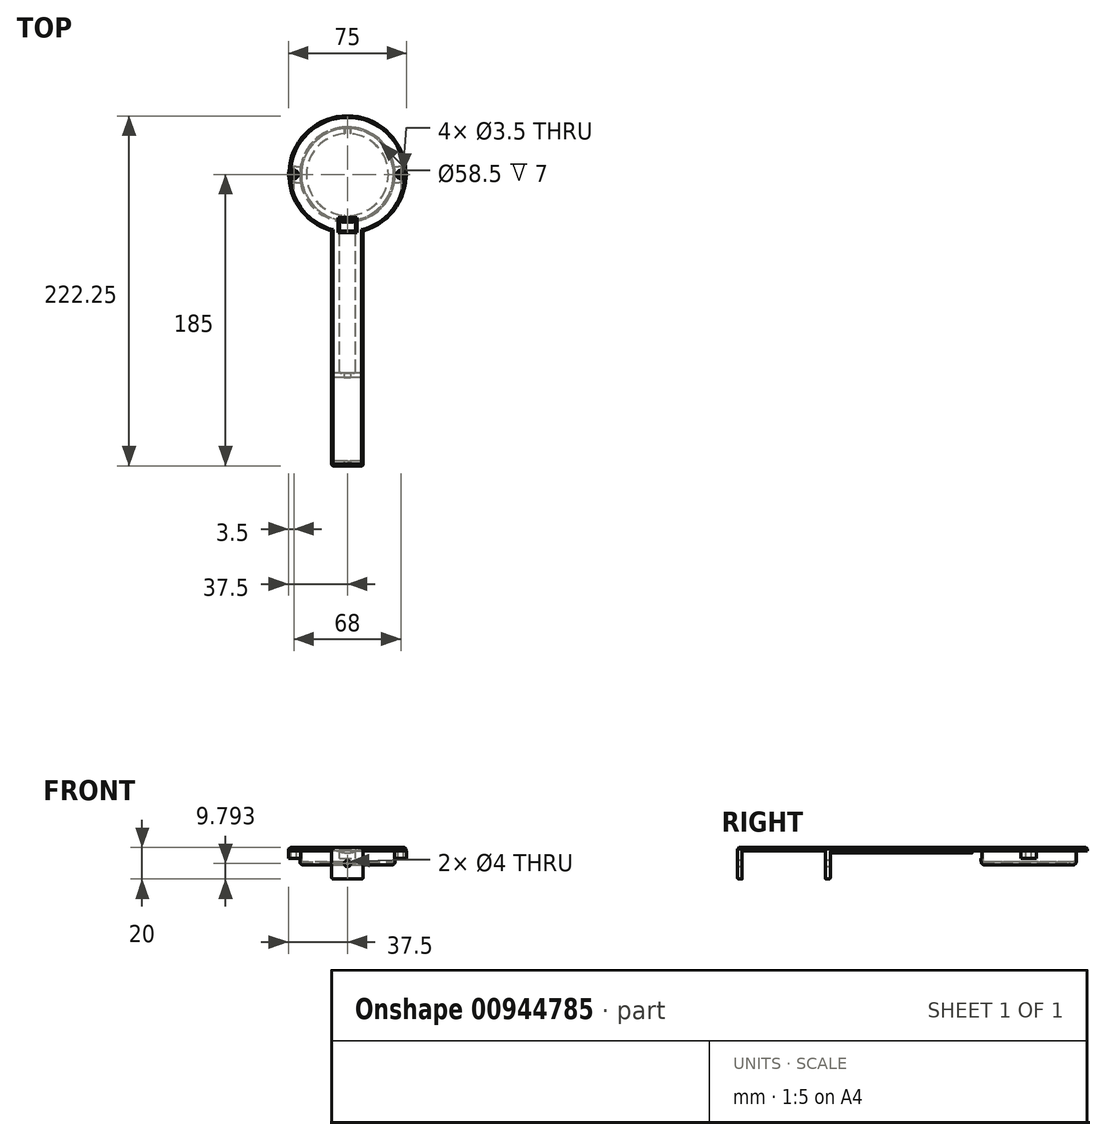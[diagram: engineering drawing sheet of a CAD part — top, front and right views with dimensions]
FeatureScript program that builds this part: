
annotation { "Feature Type Name" : "Feature", "Feature Type Description" : "" }
export const myFeature = defineFeature(function(context is Context, id is Id, definition is map)
    precondition{}
    {
        {
            var Q0;
            Q0=qCreatedBy(makeId("Top.planeOp"),FACE);
            var sketch = newSketch(context, id + "F0", { "sketchPlane" : qUnion([Q0])});
            skCircle(sketch, "E0", {"center": v(0, 0) * mm, "radius": 26 * mm});
            skCircle(sketch, "E1", {"center": v(0, 0) * mm, "radius": 29.25 * mm});
            skCircle(sketch, "E2", {"center": v(0, 0) * mm, "radius": 30.25 * mm});
            skSolve(sketch);
        }
        {
            var Q0;
            Q0=makeQuery(id+"F0.imprint","IMPRINT",FACE,{"disambiguationData":[TD([[makeQuery(id+"F0.imprint","IMPRINT",EDGE,{"derivedFrom":sQuery(id+"F0.wireOp",EDGE,"E0")}),-1.0]])]});
            extrude(context, id + "F1", {"entities" : qUnion([Q0]), "depth" : 2 * mm, "offsetDistance" : 25 * mm});
        }
        {
            var Q0;
            Q0 = qSketchRegion(id + "F0", true);
            extrude(context, id + "F2", {"entities" : qUnion([Q0]), "operationType" : NewBodyOperationType.ADD, "depth" : 9 * mm, "offsetDistance" : 25 * mm});
        }
        {
            var Q0;
            Q0=makeQuery(id+"F2.opExtrude","CAP_FACE",FACE,{"disambiguationData":[OSD([sQuery(id+"F0.wireOp",EDGE,"E1"),sQuery(id+"F0.wireOp",EDGE,"E2")])],"isStart":false});
            var sketch = newSketch(context, id + "F3", { "sketchPlane" : qUnion([Q0])});
            skPoint(sketch, "E3.0", {"position": v(0, 0) * mm});
            skCircle(sketch, "E4", {"center": v(0, 0) * mm, "radius": 29.25 * mm});
            skCircle(sketch, "E5", {"center": v(0, 0) * mm, "radius": 37.25 * mm});
            skLineSegment(sketch, "E6.bottom", {"start": v(-36.3, 8.33) * mm, "end": v(36.3, 8.33) * mm});
            skLineSegment(sketch, "E6.top", {"start": v(-36.3, -8.33) * mm, "end": v(36.3, -8.33) * mm});
            skLineSegment(sketch, "E6.left", {"start": v(-36.3, 8.33) * mm, "end": v(-36.3, -8.33) * mm});
            skLineSegment(sketch, "E6.right", {"start": v(36.3, 8.33) * mm, "end": v(36.3, -8.33) * mm});
            skLineSegment(sketch, "E7.bottom", {"start": v(-5, 36.91) * mm, "end": v(5, 36.91) * mm});
            skLineSegment(sketch, "E7.top", {"start": v(-5, -36.91) * mm, "end": v(5, -36.91) * mm});
            skLineSegment(sketch, "E7.left", {"start": v(-5, 36.91) * mm, "end": v(-5, -36.91) * mm});
            skLineSegment(sketch, "E7.right", {"start": v(5, 36.91) * mm, "end": v(5, -36.91) * mm});
            skSolve(sketch);
        }
        {
            var Q0;
            Q0=makeQuery(id+"F2.opExtrude","CAP_EDGE",EDGE,{"disambiguationData":[OSD([sQuery(id+"F0.wireOp",EDGE,"E2")])],"isStart":true});
            fillet(context, id + "F4", {"entities" : qUnion([Q0]), "radius" : 2 * mm, "tangentPropagation" : true, "allowEdgeOverflow" : false});
        }
        {
            var Q0;
            Q0=makeQuery(id+"F2.opExtrude","CAP_FACE",FACE,{"disambiguationData":[OSD([sQuery(id+"F0.wireOp",EDGE,"E1"),sQuery(id+"F0.wireOp",EDGE,"E2")])],"isStart":false});
            var sketch = newSketch(context, id + "F5", { "sketchPlane" : qUnion([Q0])});
            skPoint(sketch, "E8.0", {"position": v(0, 0) * mm});
            skLineSegment(sketch, "E9.bottom", {"start": v(-37.5, 5) * mm, "end": v(37.5, 5) * mm});
            skLineSegment(sketch, "E9.top", {"start": v(-37.5, -5) * mm, "end": v(37.5, -5) * mm});
            skLineSegment(sketch, "E9.left", {"start": v(-37.5, 5) * mm, "end": v(-37.5, -5) * mm});
            skLineSegment(sketch, "E9.right", {"start": v(37.5, 5) * mm, "end": v(37.5, -5) * mm});
            skLineSegment(sketch, "E10", {"start": v(-37.5, 0) * mm, "end": v(-34, 0) * mm, "construction": true});
            skLineSegment(sketch, "E11", {"start": v(37.5, 0) * mm, "end": v(34, 0) * mm, "construction": true});
            skCircle(sketch, "E12", {"center": v(-34, 0) * mm, "radius": 1.75 * mm});
            skCircle(sketch, "E13", {"center": v(34, 0) * mm, "radius": 1.75 * mm});
            skLineSegment(sketch, "E14.bottom", {"start": v(5, -45) * mm, "end": v(-5, -45) * mm});
            skLineSegment(sketch, "E14.top", {"start": v(5, 45) * mm, "end": v(-5, 45) * mm});
            skLineSegment(sketch, "E14.left", {"start": v(5, -45) * mm, "end": v(5, 45) * mm});
            skLineSegment(sketch, "E14.right", {"start": v(-5, -45) * mm, "end": v(-5, 45) * mm});
            skSolve(sketch);
        }
        {
            var Q0;
            {var subQ0=sQuery(id+"F5.wireOp",EDGE,"E9.left");Q0=makeQuery(id+"F5.imprint","IMPRINT",FACE,{"disambiguationData":[TD([[makeQuery(id+"F5.imprint","IMPRINT",EDGE,{"derivedFrom":subQ0}),1.0]])]});}
            var Q1;
            {var subQ0=sQuery(id+"F5.wireOp",EDGE,"E9.right");Q1=makeQuery(id+"F5.imprint","IMPRINT",FACE,{"disambiguationData":[TD([[makeQuery(id+"F5.imprint","IMPRINT",EDGE,{"derivedFrom":subQ0}),-1.0]])]});}
            extrude(context, id + "F6", {"entities" : qUnion([Q0, Q1]), "operationType" : NewBodyOperationType.ADD, "oppositeDirection" : true, "depth" : 5 * mm, "offsetDistance" : 25 * mm});
        }
        {
            var Q0;
            Q0=makeQuery(id+"F6.opExtrude","SWEPT_EDGE",EDGE,{"disambiguationData":[OSD([sQuery(id+"F5.wireOp",EDGE,"E9.top"),sQuery(id+"F5.wireOp",EDGE,"E9.right")])]});
            var Q1;
            Q1=makeQuery(id+"F6.opExtrude","SWEPT_EDGE",EDGE,{"disambiguationData":[OSD([sQuery(id+"F5.wireOp",EDGE,"E9.bottom"),sQuery(id+"F5.wireOp",EDGE,"E9.right")])]});
            var Q2;
            Q2=makeQuery(id+"F6.opExtrude","SWEPT_EDGE",EDGE,{"disambiguationData":[OSD([sQuery(id+"F5.wireOp",EDGE,"E9.top"),sQuery(id+"F5.wireOp",EDGE,"E9.left")])]});
            var Q3;
            Q3=makeQuery(id+"F6.opExtrude","SWEPT_EDGE",EDGE,{"disambiguationData":[OSD([sQuery(id+"F5.wireOp",EDGE,"E9.bottom"),sQuery(id+"F5.wireOp",EDGE,"E9.left")])]});
            fillet(context, id + "F7", {"entities" : qUnion([Q0, Q1, Q2, Q3]), "radius" : 5 * mm, "tangentPropagation" : true, "allowEdgeOverflow" : false});
        }
        {
            var Q0;
            {var subQ0=sQuery(id+"F5.wireOp",EDGE,"E14.left");var subQ1=makeQuery(id+"F2.opExtrude","CAP_EDGE",EDGE,{"disambiguationData":[OSD([sQuery(id+"F0.wireOp",EDGE,"E2")])],"isStart":false});var subQ2=makeQuery(id+"F5.imprint","INTERSECT",VERTEX,{"disambiguationData":[OD(0.0)],"derivedFrom":[subQ1,subQ0]});Q0=makeQuery(id+"F5.imprint","IMPRINT",FACE,{"disambiguationData":[TD([[makeQuery(id+"F5.imprint","IMPRINT",EDGE,{"disambiguationData":[TD([[subQ2,-1.0]])],"derivedFrom":subQ0}),1.0]])]});}
            extrude(context, id + "F8", {"entities" : qUnion([Q0]), "operationType" : NewBodyOperationType.REMOVE, "oppositeDirection" : true, "depth" : 5 * mm, "offsetDistance" : 25 * mm});
        }
        {
            var Q0;
            {var subQ0=sQuery(id+"F3.wireOp",EDGE,"E7.left");var subQ1=sQuery(id+"F3.wireOp",EDGE,"E6.bottom");var subQ2=makeQuery(id+"F3.imprint","INTERSECT",VERTEX,{"derivedFrom":[subQ1,subQ0]});Q0=makeQuery(id+"F3.imprint","IMPRINT",FACE,{"disambiguationData":[TD([[makeQuery(id+"F3.imprint","IMPRINT",EDGE,{"disambiguationData":[TD([[subQ2,-1.0]])],"derivedFrom":subQ1}),-1.0]])]});}
            var sketch = newSketch(context, id + "F9", { "sketchPlane" : qUnion([Q0])});
            skCircle(sketch, "E15.0", {"center": v(0, 0) * mm, "radius": 37.25 * mm});
            skCircle(sketch, "E15.1", {"center": v(-34, 0) * mm, "radius": 1.75 * mm});
            skCircle(sketch, "E15.2", {"center": v(34, 0) * mm, "radius": 1.75 * mm});
            skPoint(sketch, "E15.3", {"position": v(0, 0) * mm});
            skSolve(sketch);
        }
        {
            var Q0;
            Q0=makeQuery(id+"F9.imprint","IMPRINT",FACE,{"disambiguationData":[TD([[makeQuery(id+"F9.imprint","IMPRINT",EDGE,{"derivedFrom":sQuery(id+"F9.wireOp",EDGE,"E15.0")}),1.0]])]});
            var Q1;
            {var subQ0=sQuery(id+"F3.wireOp",EDGE,"E7.left");var subQ1=sQuery(id+"F3.wireOp",EDGE,"E6.bottom");var subQ2=makeQuery(id+"F3.imprint","INTERSECT",VERTEX,{"derivedFrom":[subQ1,subQ0]});Q1=makeQuery(id+"F9.imprint","IMPRINT",FACE,{"disambiguationData":[TD([[makeQuery(id+"F9.imprint","IMPRINT",EDGE,{"derivedFrom":makeQuery(id+"F3.imprint","IMPRINT",EDGE,{"disambiguationData":[TD([[subQ2,-1.0]])],"derivedFrom":subQ1})}),-1.0]])]});}
            extrude(context, id + "F10", {"entities" : qUnion([Q0, Q1]), "depth" : 2 * mm, "offsetDistance" : 25 * mm});
        }
        {
            var Q0;
            Q0=makeQuery(id+"F10.opExtrude","CAP_FACE",FACE,{"disambiguationData":[OSD([sQuery(id+"F9.wireOp",EDGE,"E15.0"),sQuery(id+"F9.wireOp",EDGE,"E15.1"),sQuery(id+"F9.wireOp",EDGE,"E15.2")])],"isStart":false});
            var sketch = newSketch(context, id + "F11", { "sketchPlane" : qUnion([Q0])});
            skLineSegment(sketch, "E16", {"start": v(34, 0) * mm, "end": v(-34, 0) * mm, "construction": true});
            skPoint(sketch, "E17.0", {"position": v(0, 0) * mm});
            skLineSegment(sketch, "E18", {"start": v(0, 0) * mm, "end": v(-10, 0) * mm, "construction": true});
            skLineSegment(sketch, "E19", {"start": v(0, 0) * mm, "end": v(10, 0) * mm, "construction": true});
            skLineSegment(sketch, "E20", {"start": v(-10, 0) * mm, "end": v(-10, 15) * mm, "construction": true});
            skLineSegment(sketch, "E21", {"start": v(-10, 15) * mm, "end": v(10, 15) * mm, "construction": true});
            skLineSegment(sketch, "E22.bottom", {"start": v(-10, 15) * mm, "end": v(10, 15) * mm});
            skLineSegment(sketch, "E22.top", {"start": v(-10, -185) * mm, "end": v(10, -185) * mm});
            skLineSegment(sketch, "E22.left", {"start": v(-10, 15) * mm, "end": v(-10, -185) * mm});
            skLineSegment(sketch, "E22.right", {"start": v(10, 15) * mm, "end": v(10, -185) * mm});
            skSolve(sketch);
        }
        {
            var Q0;
            {var subQ0=sQuery(id+"F11.wireOp",EDGE,"E22.top");Q0=makeQuery(id+"F11.imprint","IMPRINT",FACE,{"disambiguationData":[TD([[makeQuery(id+"F11.imprint","IMPRINT",EDGE,{"derivedFrom":subQ0}),1.0]])]});}
            extrude(context, id + "F12", {"entities" : qUnion([Q0]), "operationType" : NewBodyOperationType.ADD, "oppositeDirection" : true, "depth" : 2 * mm, "offsetDistance" : 25 * mm});
        }
        {
            var Q0;
            Q0=makeQuery(id+"F9.imprint","IMPRINT",FACE,{"disambiguationData":[TD([[makeQuery(id+"F9.imprint","IMPRINT",EDGE,{"derivedFrom":sQuery(id+"F9.wireOp",EDGE,"E15.0")}),1.0]])]});
            var sketch = newSketch(context, id + "F13", { "sketchPlane" : qUnion([Q0])});
            skLineSegment(sketch, "E23", {"start": v(0, 9.04) * mm, "end": v(0, -35.96) * mm, "construction": true});
            skLineSegment(sketch, "E24.bottom", {"start": v(5, -28.46) * mm, "end": v(-5, -28.46) * mm});
            skPoint(sketch, "E24.middle", {"position": v(0, -35.96) * mm});
            skLineSegment(sketch, "E25", {"start": v(5, -35.96) * mm, "end": v(-5, -35.96) * mm});
            skLineSegment(sketch, "E26", {"start": v(5, -28.46) * mm, "end": v(5, -35.96) * mm});
            skLineSegment(sketch, "E27", {"start": v(-5, -35.96) * mm, "end": v(-5, -28.46) * mm});
            skSolve(sketch);
        }
        {
            var Q0;
            Q0=makeQuery(id+"F13.imprint","IMPRINT",FACE,{"disambiguationData":[TD([[makeQuery(id+"F13.imprint","IMPRINT",EDGE,{"derivedFrom":sQuery(id+"F13.wireOp",EDGE,"E24.bottom")}),1.0]])]});
            extrude(context, id + "F14", {"entities" : qUnion([Q0]), "operationType" : NewBodyOperationType.REMOVE, "endBound" : BoundingType.UP_TO_NEXT, "depth" : 25 * mm, "offsetDistance" : 25 * mm});
        }
        {
            var Q0;
            {var subQ0=sQuery(id+"F9.wireOp",EDGE,"E15.0");Q0=makeQuery(id+"F12.boolean.opBoolean","MERGE",FACE,{"derivedFrom":[makeQuery(id+"F10.opExtrude","CAP_FACE",FACE,{"disambiguationData":[OSD([subQ0,sQuery(id+"F9.wireOp",EDGE,"E15.1"),sQuery(id+"F9.wireOp",EDGE,"E15.2")])],"isStart":false}),makeQuery(id+"F12.opExtrude","CAP_FACE",FACE,{"disambiguationData":[OSD([subQ0,sQuery(id+"F11.wireOp",EDGE,"E22.top"),sQuery(id+"F11.wireOp",EDGE,"E22.left"),sQuery(id+"F11.wireOp",EDGE,"E22.right")])],"isStart":true})]});}
            chamfer(context, id + "F15", {"entities" : qUnion([Q0]), "chamferType" : ChamferType.OFFSET_ANGLE, "width" : 1 * mm, "oppositeDirection" : false, "angle" : 45 * degree, "tangentPropagation" : true});
        }
        {
            var Q0;
            {var subQ0=sQuery(id+"F9.wireOp",EDGE,"E15.0");Q0=makeQuery(id+"F12.boolean.opBoolean","MERGE",FACE,{"derivedFrom":[makeQuery(id+"F10.opExtrude","CAP_FACE",FACE,{"disambiguationData":[OSD([subQ0,sQuery(id+"F9.wireOp",EDGE,"E15.1"),sQuery(id+"F9.wireOp",EDGE,"E15.2")])],"isStart":true}),makeQuery(id+"F12.opExtrude","CAP_FACE",FACE,{"disambiguationData":[OSD([subQ0,sQuery(id+"F11.wireOp",EDGE,"E22.top"),sQuery(id+"F11.wireOp",EDGE,"E22.left"),sQuery(id+"F11.wireOp",EDGE,"E22.right")])],"isStart":false})]});}
            var sketch = newSketch(context, id + "F16", { "sketchPlane" : qUnion([Q0])});
            skLineSegment(sketch, "E28.bottom", {"start": v(10, 185) * mm, "end": v(-10, 185) * mm});
            skLineSegment(sketch, "E28.top", {"start": v(10, 182) * mm, "end": v(-10, 182) * mm});
            skLineSegment(sketch, "E28.left", {"start": v(10, 185) * mm, "end": v(10, 182) * mm});
            skLineSegment(sketch, "E28.right", {"start": v(-10, 185) * mm, "end": v(-10, 182) * mm});
            skLineSegment(sketch, "E29.bottom", {"start": v(10, 182) * mm, "end": v(-10, 182) * mm, "construction": true});
            skLineSegment(sketch, "E29.top", {"start": v(10, 129) * mm, "end": v(-10, 129) * mm, "construction": true});
            skLineSegment(sketch, "E29.left", {"start": v(10, 182) * mm, "end": v(10, 129) * mm, "construction": true});
            skLineSegment(sketch, "E29.right", {"start": v(-10, 182) * mm, "end": v(-10, 129) * mm, "construction": true});
            skLineSegment(sketch, "E30.bottom", {"start": v(10, 129) * mm, "end": v(-10, 129) * mm});
            skLineSegment(sketch, "E30.top", {"start": v(10, 126) * mm, "end": v(-10, 126) * mm});
            skLineSegment(sketch, "E30.left", {"start": v(10, 129) * mm, "end": v(10, 126) * mm});
            skLineSegment(sketch, "E30.right", {"start": v(-10, 129) * mm, "end": v(-10, 126) * mm});
            skSolve(sketch);
        }
        {
            var Q0;
            Q0=makeQuery(id+"F16.imprint","IMPRINT",FACE,{"disambiguationData":[TD([[makeQuery(id+"F16.imprint","IMPRINT",EDGE,{"derivedFrom":sQuery(id+"F16.wireOp",EDGE,"E28.bottom")}),-1.0]])]});
            extrude(context, id + "F17", {"entities" : qUnion([Q0]), "operationType" : NewBodyOperationType.ADD, "depth" : 18 * mm, "offsetDistance" : 25 * mm});
        }
        {
            var Q0;
            Q0=makeQuery(id+"F16.imprint","IMPRINT",FACE,{"disambiguationData":[TD([[makeQuery(id+"F16.imprint","IMPRINT",EDGE,{"derivedFrom":sQuery(id+"F16.wireOp",EDGE,"E30.bottom")}),1.0]])]});
            extrude(context, id + "F18", {"entities" : qUnion([Q0]), "operationType" : NewBodyOperationType.ADD, "depth" : 18 * mm, "offsetDistance" : 25 * mm});
        }
        {
            var Q0;
            Q0=makeQuery(id+"F18.opExtrude","SWEPT_FACE",FACE,{"disambiguationData":[OSD([sQuery(id+"F16.wireOp",EDGE,"E30.top")])]});
            var Q1;
            Q1=makeQuery(id+"F18.opExtrude","CAP_EDGE",EDGE,{"disambiguationData":[OSD([sQuery(id+"F16.wireOp",EDGE,"E30.left")])],"isStart":false});
            var Q2;
            Q2=makeQuery(id+"F18.opExtrude","CAP_EDGE",EDGE,{"disambiguationData":[OSD([sQuery(id+"F16.wireOp",EDGE,"E30.right")])],"isStart":false});
            var Q3;
            Q3=makeQuery(id+"F17.boolean.opBoolean","MERGE",FACE,{"derivedFrom":[makeQuery(id+"F12.opExtrude","SWEPT_FACE",FACE,{"disambiguationData":[OSD([sQuery(id+"F11.wireOp",EDGE,"E22.top")])]}),makeQuery(id+"F17.opExtrude","SWEPT_FACE",FACE,{"disambiguationData":[OSD([sQuery(id+"F16.wireOp",EDGE,"E28.bottom")])]})]});
            var Q4;
            Q4=makeQuery(id+"F17.opExtrude","CAP_EDGE",EDGE,{"disambiguationData":[OSD([sQuery(id+"F16.wireOp",EDGE,"E28.left")])],"isStart":false});
            var Q5;
            Q5=makeQuery(id+"F17.opExtrude","CAP_EDGE",EDGE,{"disambiguationData":[OSD([sQuery(id+"F16.wireOp",EDGE,"E28.right")])],"isStart":false});
            fillet(context, id + "F19", {"entities" : qUnion([Q0, Q1, Q2, Q3, Q4, Q5]), "radius" : 1 * mm, "tangentPropagation" : true, "allowEdgeOverflow" : false});
        }
        {
            var Q0;
            Q0=makeQuery(id+"F14.boolean.opBoolean","COPY",FACE,{"derivedFrom":makeQuery(id+"F14.opExtrude","SWEPT_FACE",FACE,{"disambiguationData":[OSD([sQuery(id+"F13.wireOp",EDGE,"E25")])]})});
            var sketch = newSketch(context, id + "F20", { "sketchPlane" : qUnion([Q0])});
            skLineSegment(sketch, "E31.0", {"start": v(-5, 9) * mm, "end": v(5, 9) * mm});
            skPoint(sketch, "E31.2", {"position": v(0, 9) * mm});
            skLineSegment(sketch, "E32.top", {"start": v(5, 8.5) * mm, "end": v(-5, 8.5) * mm});
            skArc(sketch, "E33", {"start": v(-5, 8.5) * mm, "mid": v(0, 7.6) * mm, "end": v(5, 8.5) * mm});
            skLineSegment(sketch, "E34", {"start": v(5, 9) * mm, "end": v(5, 8.5) * mm});
            skLineSegment(sketch, "E35", {"start": v(-5, 8.5) * mm, "end": v(-5, 9) * mm});
            skSolve(sketch);
        }
        {
            var Q0;
            Q0=makeQuery(id+"F20.imprint","IMPRINT",FACE,{"disambiguationData":[TD([[makeQuery(id+"F20.imprint","IMPRINT",EDGE,{"derivedFrom":sQuery(id+"F20.wireOp",EDGE,"E32.top")}),1.0]])]});
            var Q1;
            Q1=makeQuery(id+"F20.imprint","IMPRINT",FACE,{"disambiguationData":[TD([[makeQuery(id+"F20.imprint","IMPRINT",EDGE,{"derivedFrom":sQuery(id+"F20.wireOp",EDGE,"E31.0")}),-1.0]])]});
            var Q2;
            Q2=makeQuery(id+"F18.opExtrude","SWEPT_FACE",FACE,{"disambiguationData":[OSD([sQuery(id+"F16.wireOp",EDGE,"E30.top")])]});
            extrude(context, id + "F21", {"entities" : qUnion([Q0, Q1]), "operationType" : NewBodyOperationType.ADD, "endBound" : BoundingType.UP_TO_SURFACE, "oppositeDirection" : true, "depth" : 25 * mm, "endBoundEntityFace" : qUnion([Q2]), "offsetDistance" : 25 * mm});
        }
        {
            var Q0;
            Q0=makeQuery(id+"F17.boolean.opBoolean","MERGE",FACE,{"derivedFrom":[makeQuery(id+"F12.opExtrude","SWEPT_FACE",FACE,{"disambiguationData":[OSD([sQuery(id+"F11.wireOp",EDGE,"E22.top")])]}),makeQuery(id+"F17.opExtrude","SWEPT_FACE",FACE,{"disambiguationData":[OSD([sQuery(id+"F16.wireOp",EDGE,"E28.bottom")])]})]});
            var sketch = newSketch(context, id + "F22", { "sketchPlane" : qUnion([Q0])});
            skLineSegment(sketch, "E36", {"start": v(9, -8) * mm, "end": v(-9, 9.59) * mm, "construction": true});
            skLineSegment(sketch, "E37", {"start": v(9, 9.59) * mm, "end": v(-9, -8) * mm, "construction": true});
            skPoint(sketch, "E38", {"position": v(0, 0.8) * mm});
            skCircle(sketch, "E39", {"center": v(0, 0.8) * mm, "radius": 2 * mm});
            skSolve(sketch);
        }
        {
            var Q0;
            Q0=makeQuery(id+"F22.imprint","IMPRINT",FACE,{"disambiguationData":[TD([[makeQuery(id+"F22.imprint","IMPRINT",EDGE,{"derivedFrom":sQuery(id+"F22.wireOp",EDGE,"E39")}),1.0]])]});
            extrude(context, id + "F23", {"entities" : qUnion([Q0]), "operationType" : NewBodyOperationType.REMOVE, "endBound" : BoundingType.THROUGH_ALL, "oppositeDirection" : true, "depth" : 25 * mm, "offsetDistance" : 25 * mm});
        }
    });
